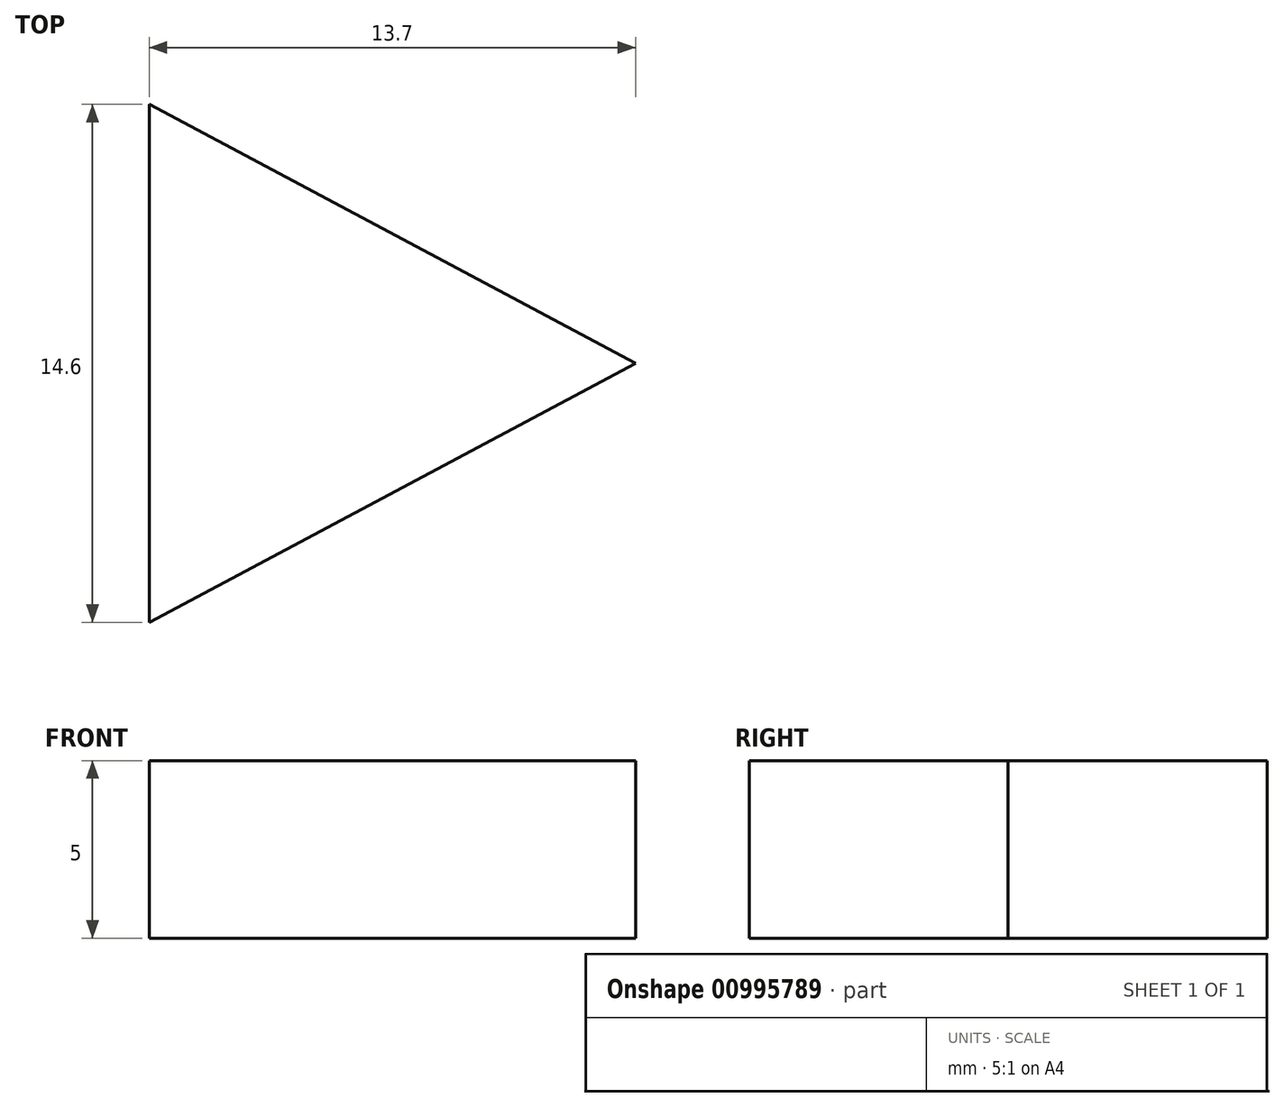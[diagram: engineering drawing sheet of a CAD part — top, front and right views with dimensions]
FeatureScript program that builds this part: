
annotation { "Feature Type Name" : "Feature", "Feature Type Description" : "" }
export const myFeature = defineFeature(function(context is Context, id is Id, definition is map)
    precondition{}
    {
        {
            var Q0;
            Q0=qCreatedBy(makeId("Top.planeOp"),FACE);
            var sketch = newSketch(context, id + "F0", { "sketchPlane" : qUnion([Q0])});
            skLineSegment(sketch, "E0", {"start": v(-5, 7.3) * mm, "end": v(-5, -7.3) * mm});
            skLineSegment(sketch, "E1", {"start": v(-5, -7.3) * mm, "end": v(8.7, 0) * mm});
            skLineSegment(sketch, "E2", {"start": v(8.7, 0) * mm, "end": v(-5, 7.3) * mm});
            skSolve(sketch);
        }
        {
            var Q0;
            Q0=makeQuery(id+"F0.imprint","IMPRINT",FACE,{"disambiguationData":[TD([[makeQuery(id+"F0.imprint","IMPRINT",EDGE,{"derivedFrom":sQuery(id+"F0.wireOp",EDGE,"E0")}),1.0]])]});
            extrude(context, id + "F1", {"entities" : qUnion([Q0]), "depth" : 5 * mm, "offsetDistance" : 25 * mm});
        }
    });
